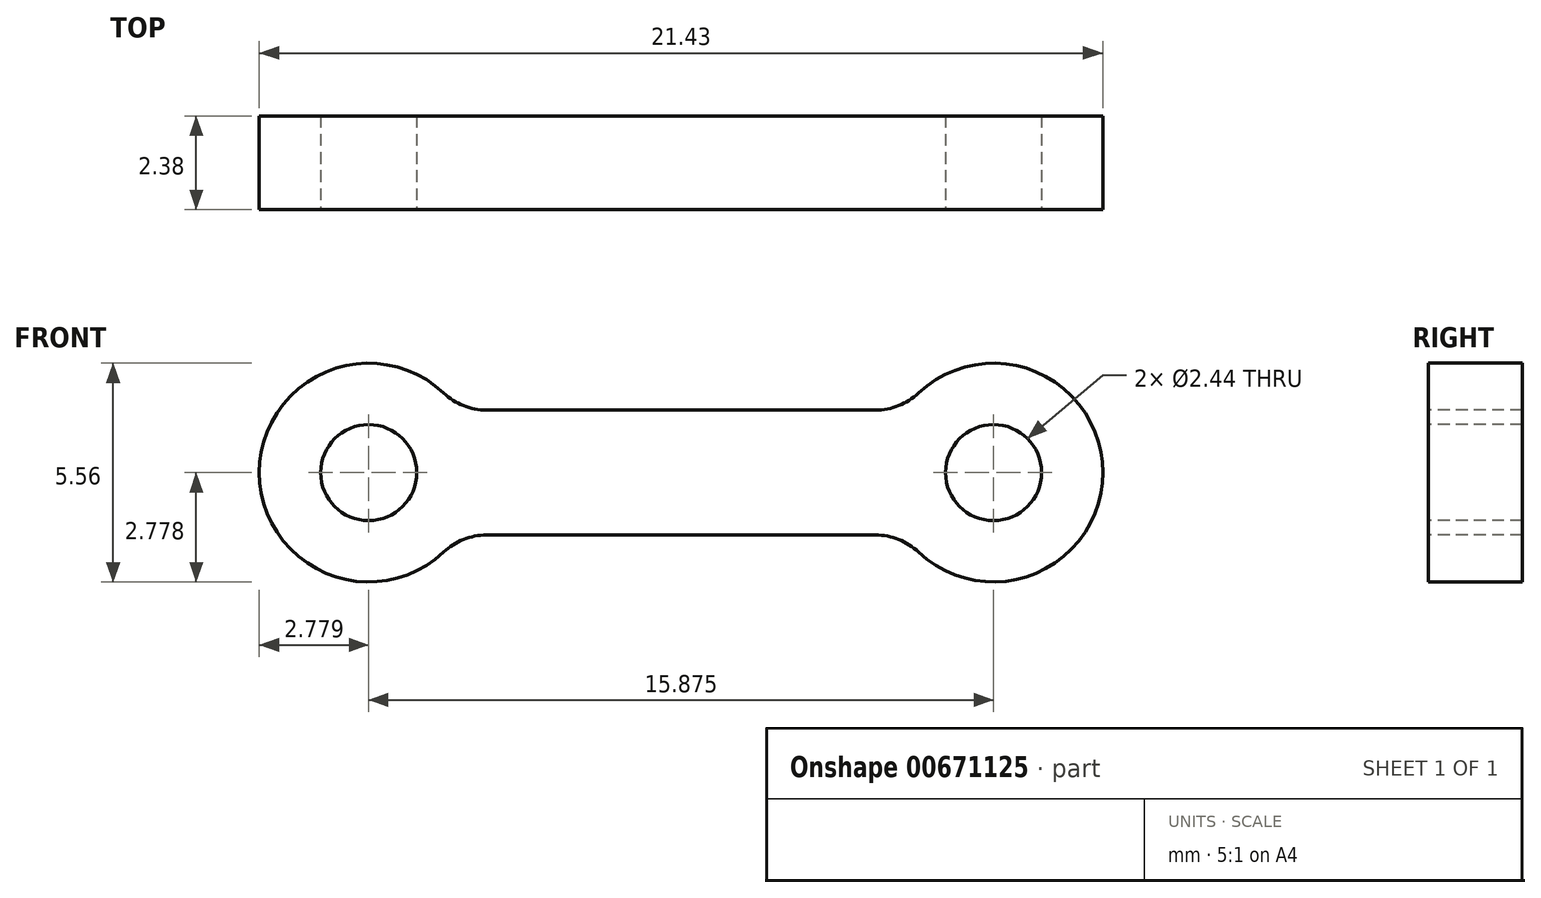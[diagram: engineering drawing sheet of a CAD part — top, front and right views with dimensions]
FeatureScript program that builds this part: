
annotation { "Feature Type Name" : "Feature", "Feature Type Description" : "" }
export const myFeature = defineFeature(function(context is Context, id is Id, definition is map)
    precondition{}
    {
        {
            var Q0;
            Q0=qCreatedBy(makeId("Top.planeOp"),FACE);
            var sketch = newSketch(context, id + "F0", { "sketchPlane" : qUnion([Q0])});
            skLineSegment(sketch, "E0.bottom", {"start": v(5.95, 23.16) * mm, "end": v(27.38, 23.16) * mm});
            skLineSegment(sketch, "E0.top", {"start": v(5.95, 20.78) * mm, "end": v(27.38, 20.78) * mm});
            skLineSegment(sketch, "E0.left", {"start": v(5.95, 23.16) * mm, "end": v(5.95, 20.78) * mm});
            skLineSegment(sketch, "E0.right", {"start": v(27.38, 23.16) * mm, "end": v(27.38, 20.78) * mm});
            skSolve(sketch);
        }
        {
            var Q0;
            Q0=qSketchRegion(id+"F0",true);
            extrude(context, id + "F1", {"entities" : qUnion([Q0]), "depth" : 5.56 * mm});
        }
        {
            var Q0;
            Q0=makeQuery(id+"F1.opExtrude","CAP_EDGE",EDGE,{"disambiguationData":[OSD([sQuery(id+"F0.wireOp",EDGE,"E0.right")])],"isStart":false});
            var Q1;
            Q1=makeQuery(id+"F1.opExtrude","CAP_EDGE",EDGE,{"disambiguationData":[OSD([sQuery(id+"F0.wireOp",EDGE,"E0.right")])],"isStart":true});
            var Q2;
            Q2=makeQuery(id+"F1.opExtrude","CAP_EDGE",EDGE,{"disambiguationData":[OSD([sQuery(id+"F0.wireOp",EDGE,"E0.left")])],"isStart":false});
            var Q3;
            Q3=makeQuery(id+"F1.opExtrude","CAP_EDGE",EDGE,{"disambiguationData":[OSD([sQuery(id+"F0.wireOp",EDGE,"E0.left")])],"isStart":true});
            fillet(context, id + "F2", {"entities" : qUnion([Q0, Q1, Q2, Q3]), "radius" : 2.78 * mm, "tangentPropagation" : true, "allowEdgeOverflow" : false});
        }
        {
            var Q0;
            Q0=makeQuery(id+"F1.opExtrude","SWEPT_FACE",FACE,{"disambiguationData":[OSD([sQuery(id+"F0.wireOp",EDGE,"E0.top")])]});
            var sketch = newSketch(context, id + "F3", { "sketchPlane" : qUnion([Q0])});
            skCircle(sketch, "E1", {"center": v(8.73, 2.78) * mm, "radius": 1.22 * mm});
            skCircle(sketch, "E2", {"center": v(24.6, 2.78) * mm, "radius": 1.22 * mm});
            skArc(sketch, "E3", {"start": v(8.73, 0) * mm, "mid": v(11.5, 2.78) * mm, "end": v(8.73, 5.56) * mm});
            skArc(sketch, "E4", {"start": v(24.6, 5.56) * mm, "mid": v(21.83, 2.78) * mm, "end": v(24.6, 0) * mm});
            skLineSegment(sketch, "E5", {"start": v(11, 4.37) * mm, "end": v(22.32, 4.37) * mm});
            skLineSegment(sketch, "E6", {"start": v(11, 1.2) * mm, "end": v(22.32, 1.2) * mm});
            skArc(sketch, "E7", {"start": v(10.64, 4.8) * mm, "mid": v(11.14, 4.48) * mm, "end": v(11.73, 4.37) * mm});
            skArc(sketch, "E8", {"start": v(11.73, 1.2) * mm, "mid": v(11.14, 1.08) * mm, "end": v(10.64, 0.76) * mm});
            skArc(sketch, "E9", {"start": v(21.6, 4.37) * mm, "mid": v(22.2, 4.48) * mm, "end": v(22.7, 4.8) * mm});
            skArc(sketch, "E10", {"start": v(22.7, 0.76) * mm, "mid": v(22.2, 1.08) * mm, "end": v(21.6, 1.2) * mm});
            skSolve(sketch);
        }
        {
            var Q0;
            Q0=makeQuery(id+"F3.imprint","IMPRINT",FACE,{"disambiguationData":[TD([[makeQuery(id+"F3.imprint","IMPRINT",EDGE,{"derivedFrom":sQuery(id+"F3.wireOp",EDGE,"E1")}),1.0]])]});
            var Q1;
            Q1=makeQuery(id+"F3.imprint","IMPRINT",FACE,{"disambiguationData":[TD([[makeQuery(id+"F3.imprint","IMPRINT",EDGE,{"derivedFrom":sQuery(id+"F3.wireOp",EDGE,"E2")}),1.0]])]});
            var Q2;
            {var subQ0=sQuery(id+"F3.wireOp",EDGE,"E7");Q2=makeQuery(id+"F3.imprint","IMPRINT",FACE,{"disambiguationData":[TD([[makeQuery(id+"F3.imprint","IMPRINT",EDGE,{"derivedFrom":subQ0}),1.0]])]});}
            var Q3;
            {var subQ0=sQuery(id+"F3.wireOp",EDGE,"E8");Q3=makeQuery(id+"F3.imprint","IMPRINT",FACE,{"disambiguationData":[TD([[makeQuery(id+"F3.imprint","IMPRINT",EDGE,{"derivedFrom":subQ0}),1.0]])]});}
            extrude(context, id + "F4", {"entities" : qUnion([Q0, Q1, Q2, Q3]), "operationType" : NewBodyOperationType.REMOVE, "oppositeDirection" : true, "depth" : 25.4 * mm});
        }
    });
